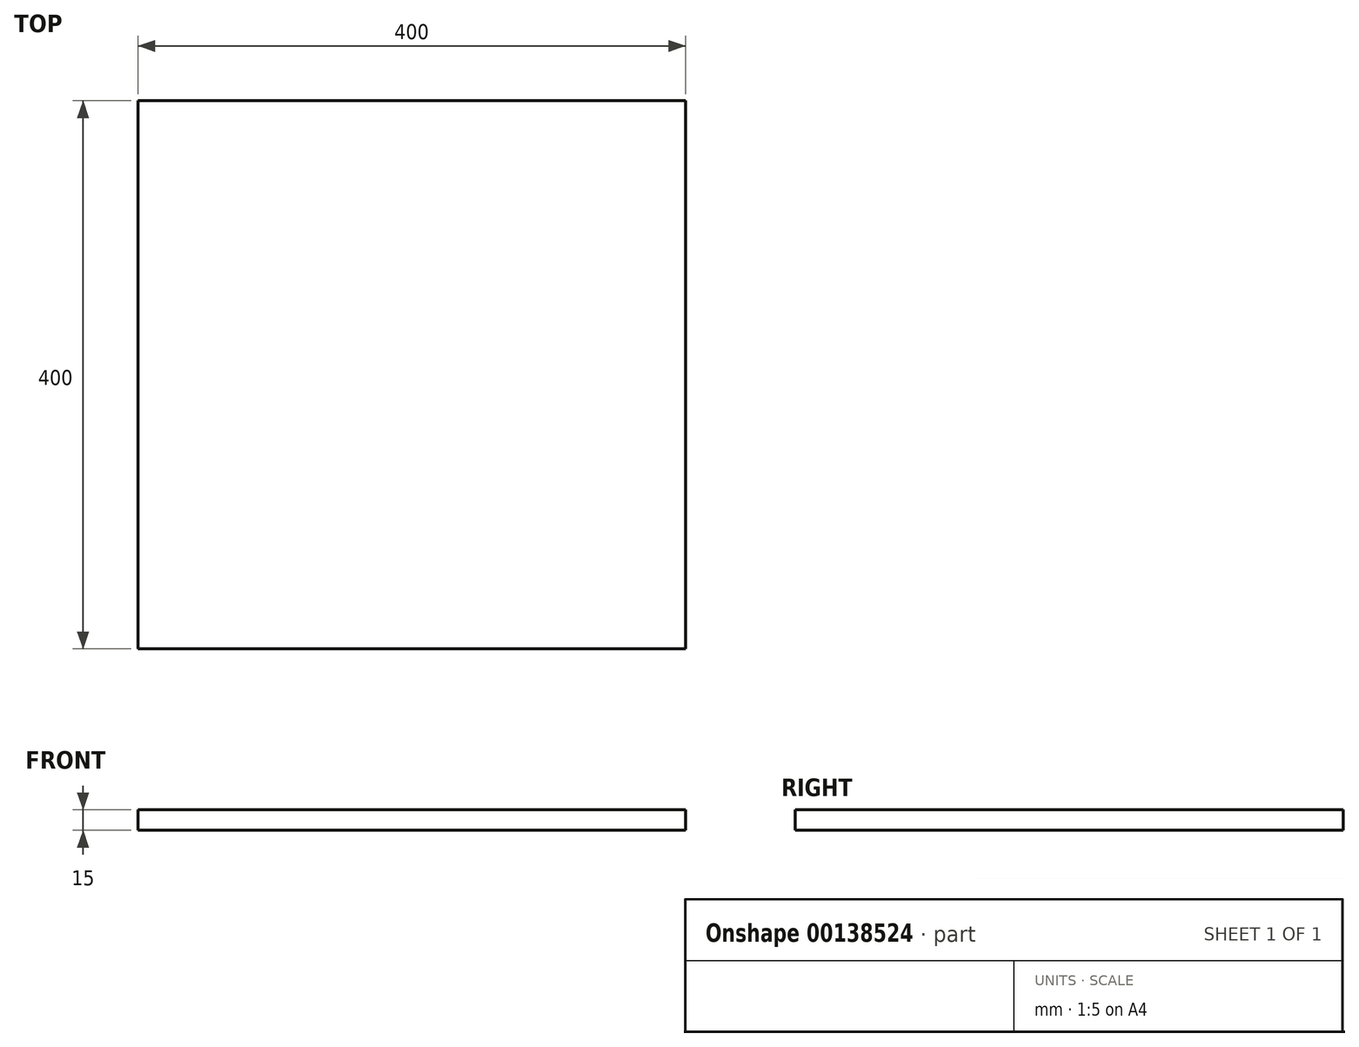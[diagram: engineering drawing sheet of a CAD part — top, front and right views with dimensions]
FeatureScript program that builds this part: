
annotation { "Feature Type Name" : "Feature", "Feature Type Description" : "" }
export const myFeature = defineFeature(function(context is Context, id is Id, definition is map)
    precondition{}
    {
        {
            var Q0;
            Q0=qCreatedBy(makeId("Top.planeOp"),FACE);
            var sketch = newSketch(context, id + "F0", { "sketchPlane" : qUnion([Q0])});
            skLineSegment(sketch, "E0.bottom", {"start": v(-200, -200) * mm, "end": v(200, -200) * mm});
            skLineSegment(sketch, "E0.top", {"start": v(-200, 200) * mm, "end": v(200, 200) * mm});
            skLineSegment(sketch, "E0.left", {"start": v(-200, -200) * mm, "end": v(-200, 200) * mm});
            skLineSegment(sketch, "E0.right", {"start": v(200, -200) * mm, "end": v(200, 200) * mm});
            skPoint(sketch, "E0.middle", {"position": v(0, 0) * mm});
            skSolve(sketch);
        }
        {
            var Q0;
            Q0=makeQuery(id+"F0.imprint","IMPRINT",FACE,{"disambiguationData":[TD([[makeQuery(id+"F0.imprint","IMPRINT",EDGE,{"derivedFrom":sQuery(id+"F0.wireOp",EDGE,"E0.bottom")}),1.0]])]});
            extrude(context, id + "F1", {"entities" : qUnion([Q0]), "depth" : 15 * mm});
        }
    });
